# Revit family: 201_PRK-_-_-B-_ +NCD-S
name_source: partatom
category: Air Terminals
units: mm (PartAtom-declared; Revit-internal decimal feet)

## family parameters
Always vertical = Yes
Cut with Voids When Loaded = No
Part Type = Normal
Room Calculation Point = Yes
Round Connector Dimension = Use Diameter
Shared = No
Work Plane-Based = No

## types (5) — shared parameters
CAT0 = Yes
CL_Location_5000 = 5000 mm  [stored 16.4042 ft]
DZ = 5 mm  [stored 0.0164042 ft]
DZ1 = 23 mm  [stored 0.0754593 ft]
DZ__ve = -5 mm  [stored -0.0164042 ft]
Description = EXPANSION BOXES TO BE MOUNTED UNDER THE NCD-S DIFFUSERS
L_ARR = 400 mm  [stored 1.31234 ft]
Manufacturer = Alnor
QmdConnectorList = 201;D
SW1 = Yes
SW2 = No
URL = http://www.ventilation-alnor.co.uk
W_ARR = 400 mm  [stored 1.31234 ft]
XRefLineVPlnId = 7453
YRefLineVPlnId = 7456
magiPartTypeId = 201
magiProductFamilyId = PRK-*-*-B-* +NCD-S
zero-valued in all types: CLBTZ, H_ARR

## per-type parameters (varying)
| type | A2 | C1 | D | DPX | DPZ | DS2 | magiProductId |
| PRK 295-295-B-125 +NCD-S | 148 mm | 200 mm  [stored 0.656168 ft] | 125 mm | 77 mm  [stored 0.252625 ft] | 100 mm  [stored 0.328084 ft] | 77 mm  [stored 0.252625 ft] | PRK-295-295-B-125 +NCD-S |
| PRK 600-600-B-200 +NCD-S | 298 mm | 400 mm  [stored 1.31234 ft] | 200 mm | 226 mm | 200 mm  [stored 0.656168 ft] | 226 mm | PRK-600-600-B-200 +NCD-S |
| PRK 525-525-B-200 +NCD-S | 260 mm | 350 mm | 200 mm | 190 mm | 175 mm | 190 mm | PRK-525-525-B-200 +NCD-S |
| PRK 450-450-B-160 +NCD-S | 223 mm  [stored 0.731627 ft] | 350 mm | 160 mm | 154 mm  [stored 0.505249 ft] | 175 mm | 154 mm  [stored 0.505249 ft] | PRK-450-450-B-160 +NCD-S |
| PRK 370-370-B-160 +NCD-S | 185 mm | 250 mm | 160 mm | 115 mm | 125 mm  [stored 0.410105 ft] | 115 mm | PRK-370-370-B-160 +NCD-S |

note: column(s) folded — value = type name in every type: MC Product Code

note: [stored X ft] marks values corroborated as IEEE doubles in the binary element streams (Revit-internal decimal feet)

## geometry (parser evidence)
native form markers: Blend x4, Sweep x2
no freeform markers — native parametric forms only
